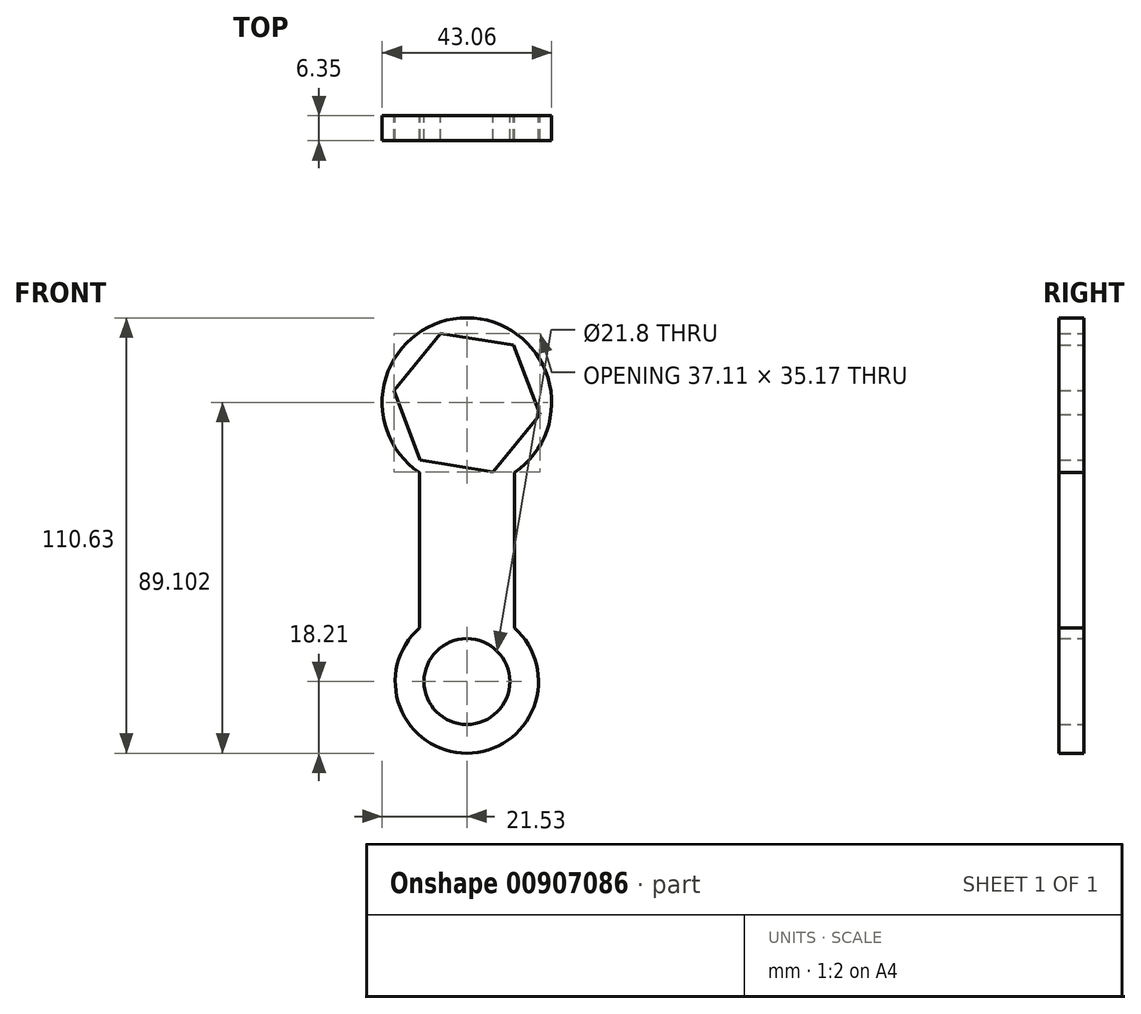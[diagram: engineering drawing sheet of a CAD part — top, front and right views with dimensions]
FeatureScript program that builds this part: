
annotation { "Feature Type Name" : "Feature", "Feature Type Description" : "" }
export const myFeature = defineFeature(function(context is Context, id is Id, definition is map)
    precondition{}
    {
        {
            var Q0;
            Q0=qCreatedBy(makeId("Front.planeOp"),FACE);
            var sketch = newSketch(context, id + "F0", { "sketchPlane" : qUnion([Q0])});
            skCircle(sketch, "E0", {"center": v(0, 0) * mm, "radius": 18.2 * mm});
            skLineSegment(sketch, "E1", {"start": v(-12.08, 13.62) * mm, "end": v(-12.08, 53.07) * mm});
            skLineSegment(sketch, "E2.MirrorCS", {"start": v(12.08, 13.62) * mm, "end": v(12.08, 53.07) * mm});
            skArc(sketch, "E3", {"start": v(-12.08, 53.07) * mm, "mid": v(0, 92.42) * mm, "end": v(12.08, 53.07) * mm});
            skArc(sketch, "E4.1.0", {"start": v(-39.92, -37) * mm, "mid": v(-80.04, -46.21) * mm, "end": v(-52, -16.07) * mm});
            skLineSegment(sketch, "E4.1.1", {"start": v(-17.83, 3.66) * mm, "end": v(-52, -16.07) * mm});
            skLineSegment(sketch, "E4.1.2", {"start": v(-5.75, -17.27) * mm, "end": v(-39.92, -37) * mm});
            skArc(sketch, "E4.2.0", {"start": v(52, -16.07) * mm, "mid": v(80.04, -46.21) * mm, "end": v(39.92, -37) * mm});
            skLineSegment(sketch, "E4.2.1", {"start": v(5.75, -17.27) * mm, "end": v(39.92, -37) * mm});
            skLineSegment(sketch, "E4.2.2", {"start": v(17.83, 3.66) * mm, "end": v(52, -16.07) * mm});
            skCircle(sketch, "E5.cCircle", {"center": v(0, 70.9) * mm, "radius": 16.28 * mm, "construction": true});
            skLineSegment(sketch, "E5.0", {"start": v(-11.9, 56.34) * mm, "end": v(-18.55, 73.93) * mm});
            skLineSegment(sketch, "E5.1", {"start": v(-18.55, 73.93) * mm, "end": v(-6.65, 88.48) * mm});
            skLineSegment(sketch, "E5.2", {"start": v(-6.65, 88.48) * mm, "end": v(11.9, 85.44) * mm});
            skLineSegment(sketch, "E5.3", {"start": v(11.9, 85.44) * mm, "end": v(18.55, 67.86) * mm});
            skLineSegment(sketch, "E5.4", {"start": v(18.55, 67.86) * mm, "end": v(6.65, 53.3) * mm});
            skLineSegment(sketch, "E5.5", {"start": v(6.65, 53.3) * mm, "end": v(-11.9, 56.34) * mm});
            skPoint(sketch, "E5.0.midPoint", {"position": v(-15.23, 65.14) * mm});
            skCircle(sketch, "E6.cCircle", {"center": v(-61.4, -35.45) * mm, "radius": 16.28 * mm, "construction": true});
            skLineSegment(sketch, "E6.0", {"start": v(-60.43, -54.22) * mm, "end": v(-77.17, -45.67) * mm});
            skLineSegment(sketch, "E6.1", {"start": v(-77.17, -45.67) * mm, "end": v(-78.14, -26.9) * mm});
            skLineSegment(sketch, "E6.2", {"start": v(-78.14, -26.9) * mm, "end": v(-62.36, -16.67) * mm});
            skLineSegment(sketch, "E6.3", {"start": v(-62.36, -16.67) * mm, "end": v(-45.62, -25.22) * mm});
            skLineSegment(sketch, "E6.4", {"start": v(-45.62, -25.22) * mm, "end": v(-44.65, -44) * mm});
            skLineSegment(sketch, "E6.5", {"start": v(-44.65, -44) * mm, "end": v(-60.43, -54.22) * mm});
            skPoint(sketch, "E6.0.midPoint", {"position": v(-68.8, -49.95) * mm});
            skCircle(sketch, "E7.cCircle", {"center": v(61.4, -35.45) * mm, "radius": 16.28 * mm, "construction": true});
            skLineSegment(sketch, "E7.0", {"start": v(66.94, -53.4) * mm, "end": v(48.61, -49.23) * mm});
            skLineSegment(sketch, "E7.1", {"start": v(48.61, -49.23) * mm, "end": v(43.06, -31.27) * mm});
            skLineSegment(sketch, "E7.2", {"start": v(43.06, -31.27) * mm, "end": v(55.85, -17.48) * mm});
            skLineSegment(sketch, "E7.3", {"start": v(55.85, -17.48) * mm, "end": v(74.18, -21.66) * mm});
            skLineSegment(sketch, "E7.4", {"start": v(74.18, -21.66) * mm, "end": v(79.72, -39.63) * mm});
            skLineSegment(sketch, "E7.5", {"start": v(79.72, -39.63) * mm, "end": v(66.94, -53.4) * mm});
            skPoint(sketch, "E7.0.midPoint", {"position": v(57.77, -51.32) * mm});
            skCircle(sketch, "E8", {"center": v(0, 0) * mm, "radius": 10.9 * mm});
            skSolve(sketch);
        }
        {
            var Q0;
            {var subQ1=sQuery(id+"F0.wireOp",EDGE,"E1");Q0=makeQuery(id+"F0.imprint","IMPRINT",FACE,{"disambiguationData":[TD([[makeQuery(id+"F0.imprint","IMPRINT",EDGE,{"derivedFrom":subQ1}),-1.0]])]});}
            var Q1;
            Q1=makeQuery(id+"F0.imprint","IMPRINT",FACE,{"disambiguationData":[TD([[makeQuery(id+"F0.imprint","IMPRINT",EDGE,{"derivedFrom":sQuery(id+"F0.wireOp",EDGE,"E4.2.0")}),-1.0]])]});
            var Q2;
            Q2=makeQuery(id+"F0.imprint","IMPRINT",FACE,{"disambiguationData":[TD([[makeQuery(id+"F0.imprint","IMPRINT",EDGE,{"derivedFrom":sQuery(id+"F0.wireOp",EDGE,"E4.1.0")}),-1.0]])]});
            var Q3;
            Q3=makeQuery(id+"F0.imprint","IMPRINT",FACE,{"disambiguationData":[TD([[makeQuery(id+"F0.imprint","IMPRINT",EDGE,{"derivedFrom":sQuery(id+"F0.wireOp",EDGE,"E8")}),-1.0]])]});
            extrude(context, id + "F1", {"entities" : qUnion([Q0, Q1, Q2, Q3]), "depth" : 6.35 * mm, "offsetDistance" : 25 * mm});
        }
    });
